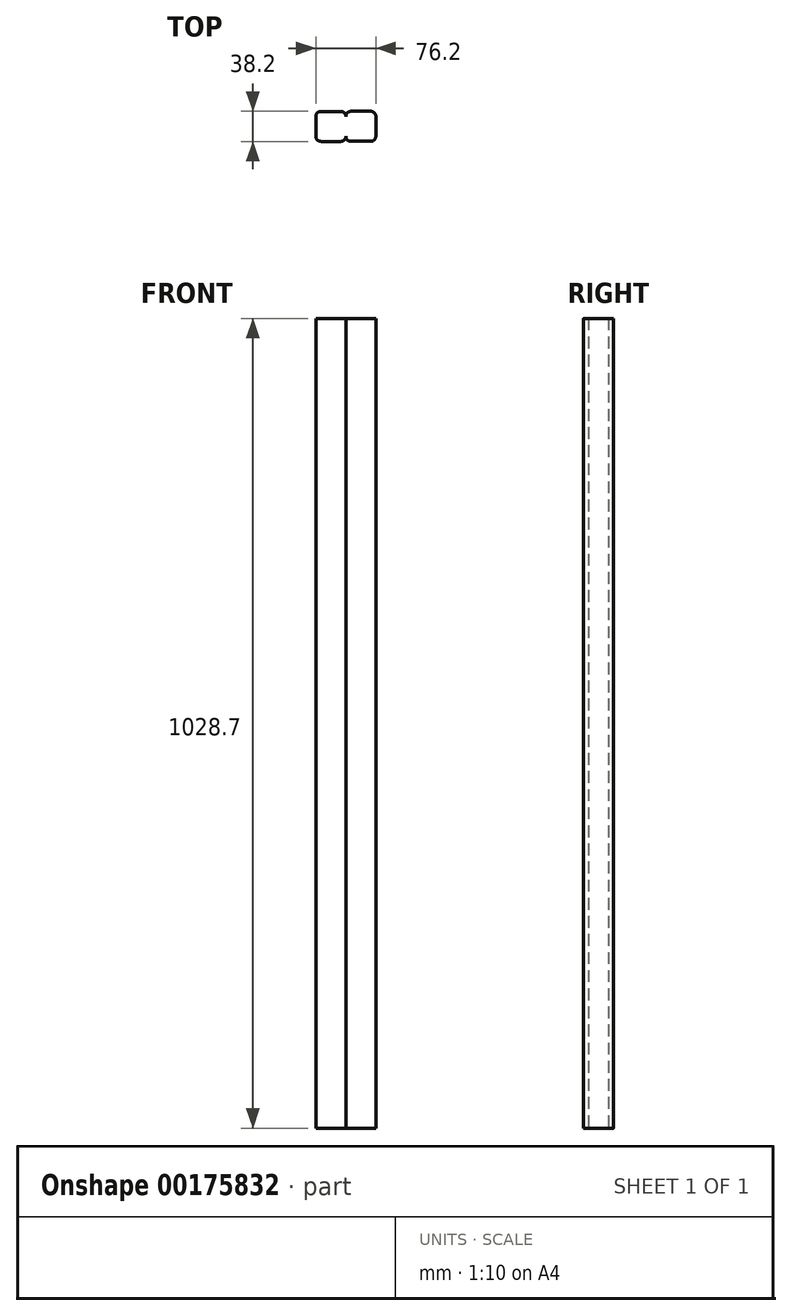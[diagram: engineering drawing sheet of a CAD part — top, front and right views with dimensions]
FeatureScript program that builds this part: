
annotation { "Feature Type Name" : "Feature", "Feature Type Description" : "" }
export const myFeature = defineFeature(function(context is Context, id is Id, definition is map)
    precondition{}
    {
        {
            var Q0;
            Q0=qCreatedBy(makeId("Top.planeOp"),FACE);
            var sketch = newSketch(context, id + "F0", { "sketchPlane" : qUnion([Q0])});
            skLineSegment(sketch, "E0.bottom", {"start": v(-6.35, 18.95) * mm, "end": v(-31.75, 18.95) * mm});
            skLineSegment(sketch, "E0.top", {"start": v(-6.35, -19.15) * mm, "end": v(-31.75, -19.15) * mm});
            skLineSegment(sketch, "E0.left", {"start": v(0, 12.6) * mm, "end": v(0, -12.8) * mm});
            skLineSegment(sketch, "E0.right", {"start": v(-38.1, 12.6) * mm, "end": v(-38.1, -12.8) * mm});
            skPoint(sketch, "E0.middle", {"position": v(-19.05, -0.1) * mm});
            skPoint(sketch, "E1.visualSharp", {"position": v(-38.1, 18.95) * mm});
            skArc(sketch, "E1.filletArc", {"start": v(-31.75, 18.95) * mm, "mid": v(-36.24, 17.09) * mm, "end": v(-38.1, 12.6) * mm});
            skPoint(sketch, "E2.visualSharp", {"position": v(0, 18.95) * mm});
            skArc(sketch, "E2.filletArc", {"start": v(0, 12.6) * mm, "mid": v(-1.86, 17.09) * mm, "end": v(-6.35, 18.95) * mm});
            skPoint(sketch, "E3.visualSharp", {"position": v(0, -19.15) * mm});
            skArc(sketch, "E3.filletArc", {"start": v(-6.35, -19.15) * mm, "mid": v(-1.86, -17.3) * mm, "end": v(0, -12.8) * mm});
            skPoint(sketch, "E4.visualSharp", {"position": v(-38.1, -19.15) * mm});
            skArc(sketch, "E4.filletArc", {"start": v(-38.1, -12.8) * mm, "mid": v(-36.24, -17.3) * mm, "end": v(-31.75, -19.15) * mm});
            skLineSegment(sketch, "E5.bottom", {"start": v(31.75, 19.05) * mm, "end": v(6.35, 19.05) * mm});
            skLineSegment(sketch, "E5.top", {"start": v(31.75, -19.05) * mm, "end": v(6.35, -19.05) * mm});
            skLineSegment(sketch, "E5.left", {"start": v(38.1, 12.7) * mm, "end": v(38.1, -12.7) * mm});
            skLineSegment(sketch, "E5.right", {"start": v(0, 12.7) * mm, "end": v(0, -12.7) * mm});
            skPoint(sketch, "E5.middle", {"position": v(19.05, 0) * mm});
            skPoint(sketch, "E6.visualSharp", {"position": v(0, 19.05) * mm});
            skArc(sketch, "E6.filletArc", {"start": v(6.35, 19.05) * mm, "mid": v(1.86, 17.2) * mm, "end": v(0, 12.7) * mm});
            skPoint(sketch, "E7.visualSharp", {"position": v(38.1, 19.05) * mm});
            skArc(sketch, "E7.filletArc", {"start": v(38.1, 12.7) * mm, "mid": v(36.24, 17.2) * mm, "end": v(31.75, 19.05) * mm});
            skPoint(sketch, "E8.visualSharp", {"position": v(38.1, -19.05) * mm});
            skArc(sketch, "E8.filletArc", {"start": v(31.75, -19.05) * mm, "mid": v(36.24, -17.2) * mm, "end": v(38.1, -12.7) * mm});
            skPoint(sketch, "E9.visualSharp", {"position": v(0, -19.05) * mm});
            skArc(sketch, "E9.filletArc", {"start": v(0, -12.7) * mm, "mid": v(1.86, -17.2) * mm, "end": v(6.35, -19.05) * mm});
            skSolve(sketch);
        }
        {
            var Q0;
            Q0 = qSketchRegion(id + "F0", true);
            extrude(context, id + "F1", {"entities" : qUnion([Q0]), "depth" : 1028.7 * mm, "offsetDistance" : 25.4 * mm});
        }
    });
